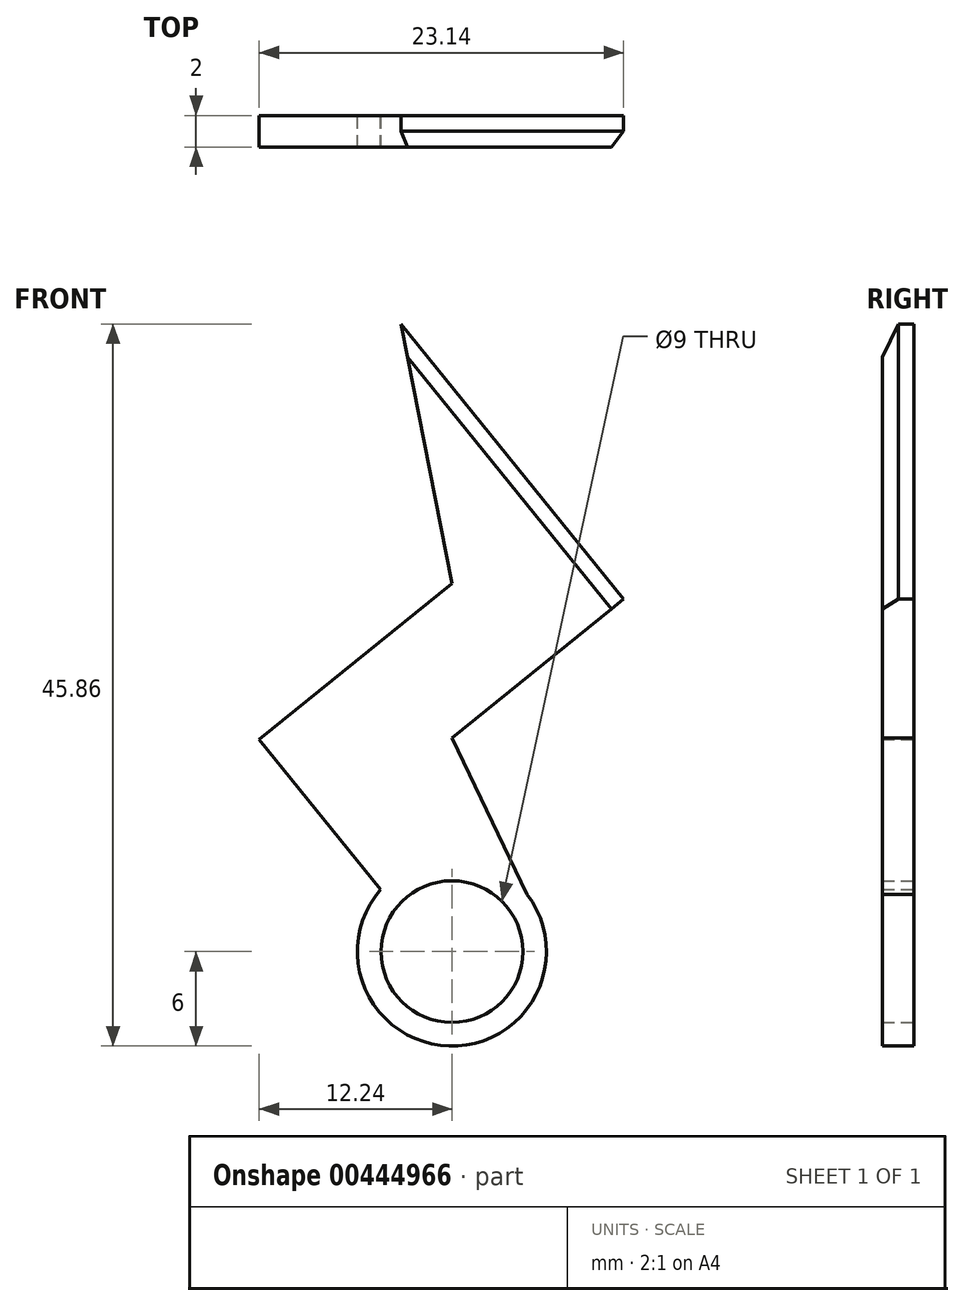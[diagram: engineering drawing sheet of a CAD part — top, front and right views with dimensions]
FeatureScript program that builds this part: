
annotation { "Feature Type Name" : "Feature", "Feature Type Description" : "" }
export const myFeature = defineFeature(function(context is Context, id is Id, definition is map)
    precondition{}
    {
        {
            var Q0;
            Q0=qCreatedBy(makeId("Front.planeOp"),FACE);
            var sketch = newSketch(context, id + "F0", { "sketchPlane" : qUnion([Q0])});
            skCircle(sketch, "E0", {"center": v(0, 0) * mm, "radius": 4.5 * mm});
            skArc(sketch, "E1", {"start": v(-4.53, 3.94) * mm, "mid": v(-0.2, -6) * mm, "end": v(4.77, 3.64) * mm});
            skLineSegment(sketch, "E2", {"start": v(-4.53, 3.94) * mm, "end": v(-12.24, 13.47) * mm});
            skLineSegment(sketch, "E3", {"start": v(-12.24, 13.47) * mm, "end": v(0, 23.38) * mm});
            skLineSegment(sketch, "E4", {"start": v(0, 23.38) * mm, "end": v(-3.23, 39.86) * mm});
            skLineSegment(sketch, "E5", {"start": v(-3.23, 39.86) * mm, "end": v(10.9, 22.4) * mm});
            skLineSegment(sketch, "E6", {"start": v(10.9, 22.4) * mm, "end": v(0, 13.58) * mm});
            skLineSegment(sketch, "E7", {"start": v(0, 13.58) * mm, "end": v(4.77, 3.64) * mm});
            skSolve(sketch);
        }
        {
            var Q0;
            Q0 = qSketchRegion(id + "F0", true);
            extrude(context, id + "F1", {"entities" : qUnion([Q0]), "depth" : 2 * mm});
        }
        {
            var Q0;
            Q0=makeQuery(id+"F1.opExtrude","CAP_EDGE",EDGE,{"disambiguationData":[OSD([sQuery(id+"F0.wireOp",EDGE,"E5")])],"isStart":false});
            chamfer(context, id + "F2", {"entities" : qUnion([Q0]), "width" : 1 * mm, "tangentPropagation" : true});
        }
    });
